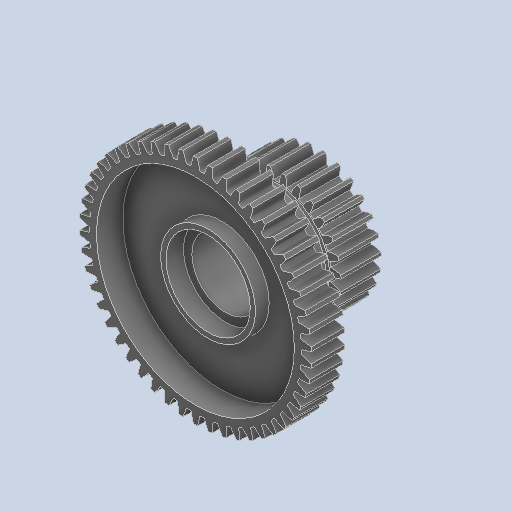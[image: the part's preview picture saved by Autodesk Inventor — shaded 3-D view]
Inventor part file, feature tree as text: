
AUTODESK INVENTOR PART (.ipt)
format: ipt  version: 2024.2 (Build 282272000, 272)  size: 591,360 bytes
history: native  units: in
note: dims shown in document units (in); Inventor stores cm internally (conversion verified against a paired STEP export)
features: chamfer x1
ambient origin geometry x8: Origin, YZ Plane, XZ Plane, XY Plane, X Axis, Y Axis, Z Axis, Center Point
bodies: Solid1 (feature_tree)
feature tree (1):
  chamfer  "Chamfer2"  [1 undecoded]
note: 1 required parameter value undecoded (feature->parameter linkage not recoverable at this tier; creation-order binding heuristic only, values carry confidence <= 0.55)
